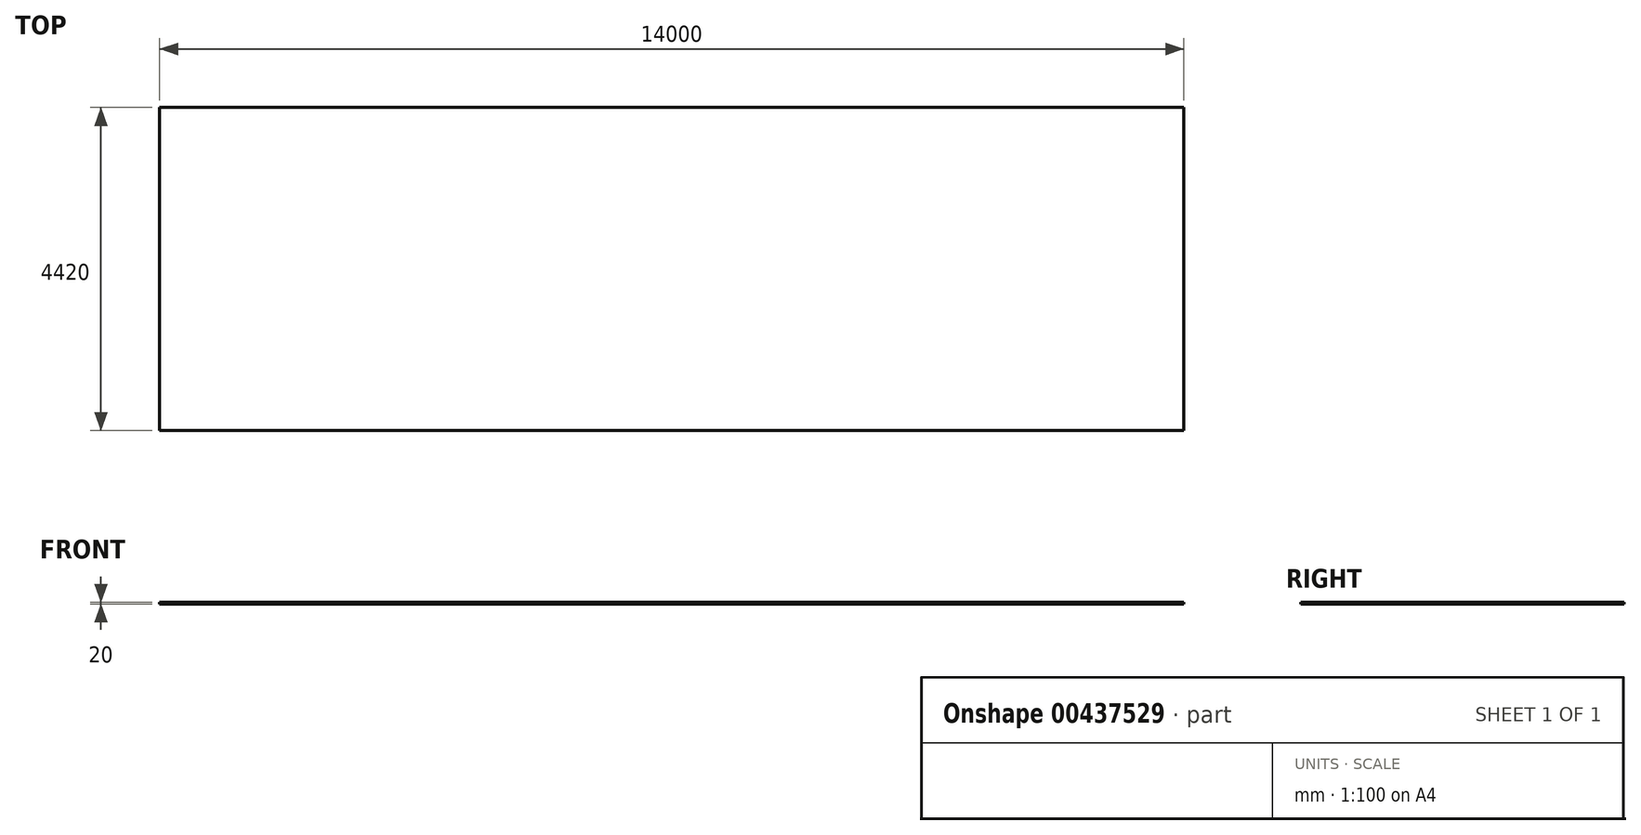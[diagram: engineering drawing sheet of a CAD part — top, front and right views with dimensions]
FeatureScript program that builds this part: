
annotation { "Feature Type Name" : "Feature", "Feature Type Description" : "" }
export const myFeature = defineFeature(function(context is Context, id is Id, definition is map)
    precondition{}
    {
        {
            var Q0;
            Q0=qCreatedBy(makeId("Top.planeOp"),FACE);
            var sketch = newSketch(context, id + "F0", { "sketchPlane" : qUnion([Q0])});
            skLineSegment(sketch, "E0.bottom", {"start": v(-7000, 2210) * mm, "end": v(7000, 2210) * mm});
            skLineSegment(sketch, "E0.top", {"start": v(-7000, -2210) * mm, "end": v(7000, -2210) * mm});
            skLineSegment(sketch, "E0.left", {"start": v(-7000, 2210) * mm, "end": v(-7000, -2210) * mm});
            skLineSegment(sketch, "E0.right", {"start": v(7000, 2210) * mm, "end": v(7000, -2210) * mm});
            skPoint(sketch, "E0.middle", {"position": v(0, 0) * mm});
            skSolve(sketch);
        }
        {
            var Q0;
            Q0 = qSketchRegion(id + "F0", true);
            extrude(context, id + "F1", {"entities" : qUnion([Q0]), "depth" : 20 * mm});
        }
    });
